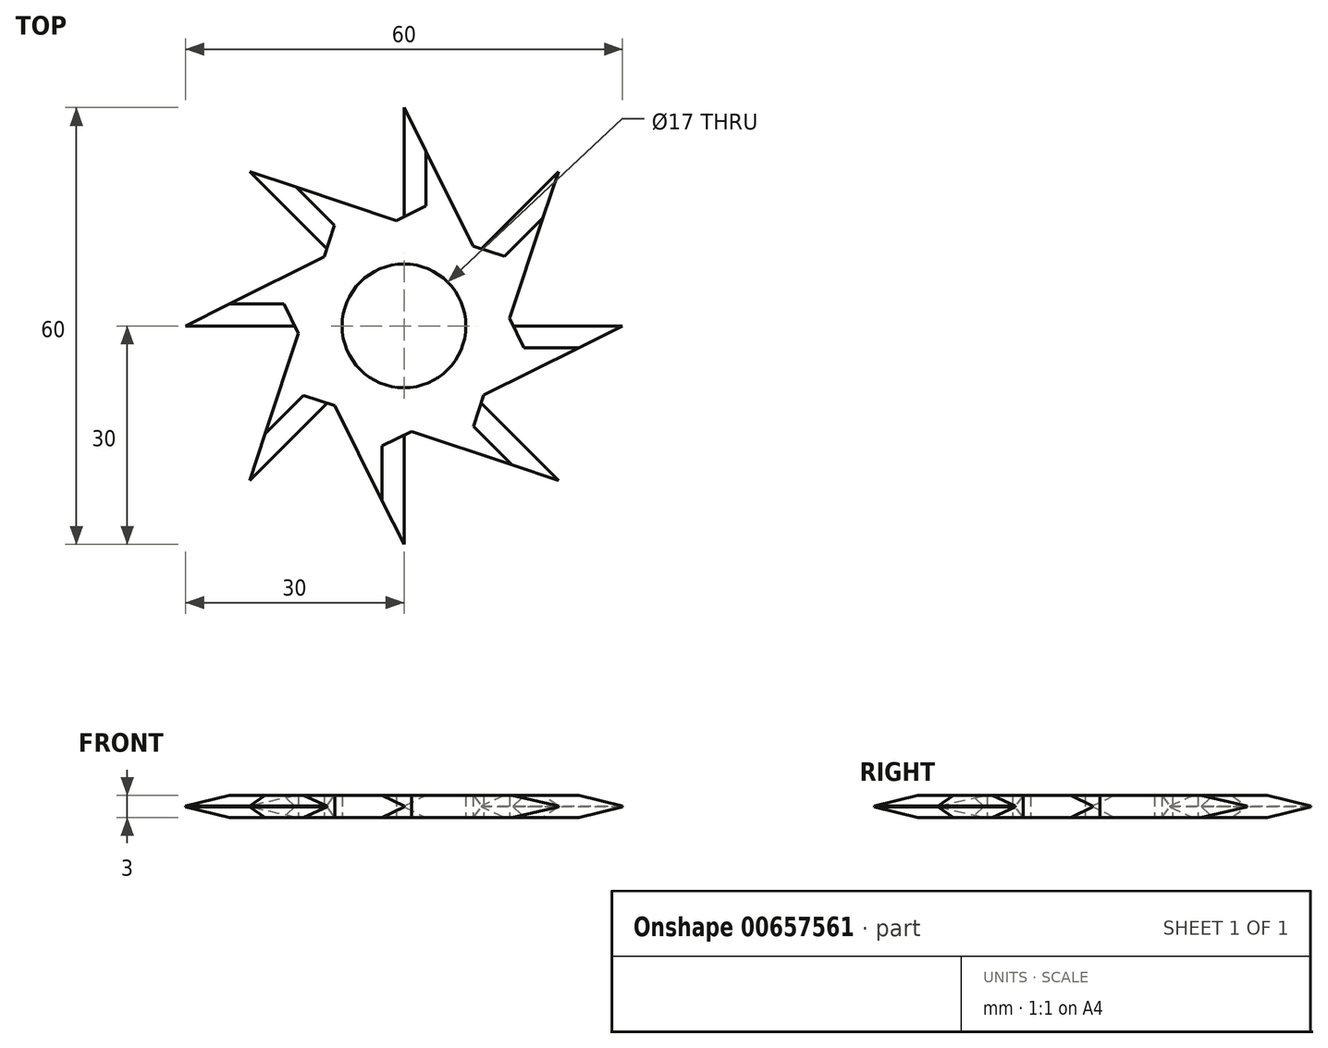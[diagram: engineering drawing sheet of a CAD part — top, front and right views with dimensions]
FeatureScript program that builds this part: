
annotation { "Feature Type Name" : "Feature", "Feature Type Description" : "" }
export const myFeature = defineFeature(function(context is Context, id is Id, definition is map)
    precondition{}
    {
        {
            var Q0;
            Q0=qCreatedBy(makeId("Top.planeOp"),FACE);
            var sketch = newSketch(context, id + "F0", { "sketchPlane" : qUnion([Q0])});
            skLineSegment(sketch, "E0", {"start": v(0, 0) * mm, "end": v(21.21, -21.21) * mm, "construction": true});
            skLineSegment(sketch, "E1", {"start": v(0, 0) * mm, "end": v(-21.21, 21.21) * mm, "construction": true});
            skLineSegment(sketch, "E2", {"start": v(0, 0) * mm, "end": v(21.21, 21.21) * mm, "construction": true});
            skLineSegment(sketch, "E3", {"start": v(21.21, 21.21) * mm, "end": v(0, 0) * mm, "construction": true});
            skLineSegment(sketch, "E4", {"start": v(0, 0) * mm, "end": v(-21.21, -21.21) * mm, "construction": true});
            skCircle(sketch, "E5", {"center": v(0, 0) * mm, "radius": 15 * mm, "construction": true});
            skCircle(sketch, "E6", {"center": v(0, 0) * mm, "radius": 30 * mm, "construction": true});
            skLineSegment(sketch, "E7", {"start": v(0, 15) * mm, "end": v(0, 30) * mm});
            skLineSegment(sketch, "E8", {"start": v(0, 30) * mm, "end": v(15, 0) * mm});
            skLineSegment(sketch, "E9", {"start": v(15, 0) * mm, "end": v(30, 0) * mm});
            skLineSegment(sketch, "E10", {"start": v(30, 0) * mm, "end": v(0, -15) * mm});
            skLineSegment(sketch, "E11", {"start": v(0, -15) * mm, "end": v(0, -30) * mm});
            skLineSegment(sketch, "E12", {"start": v(0, -30) * mm, "end": v(-15, 0) * mm});
            skLineSegment(sketch, "E13", {"start": v(-15, 0) * mm, "end": v(-30, 0) * mm});
            skLineSegment(sketch, "E14", {"start": v(-30, 0) * mm, "end": v(0, 15) * mm});
            skLineSegment(sketch, "E15", {"start": v(21.21, 21.21) * mm, "end": v(10.6, 10.6) * mm});
            skLineSegment(sketch, "E16", {"start": v(10.6, 10.6) * mm, "end": v(-21.21, 21.21) * mm});
            skLineSegment(sketch, "E17", {"start": v(-10.6, 10.6) * mm, "end": v(-21.21, 21.21) * mm});
            skLineSegment(sketch, "E18", {"start": v(-10.6, 10.6) * mm, "end": v(-21.21, -21.21) * mm});
            skLineSegment(sketch, "E19", {"start": v(-10.6, -10.6) * mm, "end": v(21.21, -21.21) * mm});
            skLineSegment(sketch, "E20", {"start": v(21.21, -21.21) * mm, "end": v(10.6, -10.6) * mm});
            skLineSegment(sketch, "E21", {"start": v(10.6, -10.6) * mm, "end": v(21.21, 21.21) * mm});
            skLineSegment(sketch, "E22", {"start": v(-21.21, -21.21) * mm, "end": v(-10.6, -10.6) * mm});
            skCircle(sketch, "E23", {"center": v(0, 0) * mm, "radius": 8.5 * mm});
            skSolve(sketch);
        }
        {
            var Q0;
            Q0=makeQuery(id+"F0.imprint","IMPRINT",FACE,{"disambiguationData":[TD([[makeQuery(id+"F0.imprint","IMPRINT",EDGE,{"derivedFrom":sQuery(id+"F0.wireOp",EDGE,"E23")}),-1.0]])]});
            var Q1;
            {var subQ5=sQuery(id+"F0.wireOp",EDGE,"E22");Q1=makeQuery(id+"F0.imprint","IMPRINT",FACE,{"disambiguationData":[TD([[makeQuery(id+"F0.imprint","IMPRINT",EDGE,{"derivedFrom":subQ5}),1.0]])]});}
            var Q2;
            {var subQ0=sQuery(id+"F0.wireOp",EDGE,"E11");Q2=makeQuery(id+"F0.imprint","IMPRINT",FACE,{"disambiguationData":[TD([[makeQuery(id+"F0.imprint","IMPRINT",EDGE,{"derivedFrom":subQ0}),-1.0]])]});}
            var Q3;
            {var subQ5=sQuery(id+"F0.wireOp",EDGE,"E20");Q3=makeQuery(id+"F0.imprint","IMPRINT",FACE,{"disambiguationData":[TD([[makeQuery(id+"F0.imprint","IMPRINT",EDGE,{"derivedFrom":subQ5}),1.0]])]});}
            var Q4;
            {var subQ0=sQuery(id+"F0.wireOp",EDGE,"E9");Q4=makeQuery(id+"F0.imprint","IMPRINT",FACE,{"disambiguationData":[TD([[makeQuery(id+"F0.imprint","IMPRINT",EDGE,{"derivedFrom":subQ0}),-1.0]])]});}
            var Q5;
            {var subQ5=sQuery(id+"F0.wireOp",EDGE,"E15");Q5=makeQuery(id+"F0.imprint","IMPRINT",FACE,{"disambiguationData":[TD([[makeQuery(id+"F0.imprint","IMPRINT",EDGE,{"derivedFrom":subQ5}),1.0]])]});}
            var Q6;
            {var subQ0=sQuery(id+"F0.wireOp",EDGE,"E7");Q6=makeQuery(id+"F0.imprint","IMPRINT",FACE,{"disambiguationData":[TD([[makeQuery(id+"F0.imprint","IMPRINT",EDGE,{"derivedFrom":subQ0}),-1.0]])]});}
            var Q7;
            {var subQ5=sQuery(id+"F0.wireOp",EDGE,"E17");Q7=makeQuery(id+"F0.imprint","IMPRINT",FACE,{"disambiguationData":[TD([[makeQuery(id+"F0.imprint","IMPRINT",EDGE,{"derivedFrom":subQ5}),-1.0]])]});}
            var Q8;
            {var subQ0=sQuery(id+"F0.wireOp",EDGE,"E13");Q8=makeQuery(id+"F0.imprint","IMPRINT",FACE,{"disambiguationData":[TD([[makeQuery(id+"F0.imprint","IMPRINT",EDGE,{"derivedFrom":subQ0}),-1.0]])]});}
            extrude(context, id + "F1", {"entities" : qUnion([Q0, Q1, Q2, Q3, Q4, Q5, Q6, Q7, Q8]), "depth" : 3 * mm, "offsetDistance" : 25 * mm});
        }
        {
            var Q0;
            Q0=makeQuery(id+"F1.opExtrude","CAP_EDGE",EDGE,{"disambiguationData":[OSD([sQuery(id+"F0.wireOp",EDGE,"E17")])],"isStart":false});
            var Q1;
            Q1=makeQuery(id+"F1.opExtrude","CAP_EDGE",EDGE,{"disambiguationData":[OSD([sQuery(id+"F0.wireOp",EDGE,"E13")])],"isStart":false});
            var Q2;
            Q2=makeQuery(id+"F1.opExtrude","CAP_EDGE",EDGE,{"disambiguationData":[OSD([sQuery(id+"F0.wireOp",EDGE,"E22")])],"isStart":false});
            var Q3;
            Q3=makeQuery(id+"F1.opExtrude","CAP_EDGE",EDGE,{"disambiguationData":[OSD([sQuery(id+"F0.wireOp",EDGE,"E11")])],"isStart":false});
            var Q4;
            Q4=makeQuery(id+"F1.opExtrude","CAP_EDGE",EDGE,{"disambiguationData":[OSD([sQuery(id+"F0.wireOp",EDGE,"E20")])],"isStart":false});
            var Q5;
            Q5=makeQuery(id+"F1.opExtrude","CAP_EDGE",EDGE,{"disambiguationData":[OSD([sQuery(id+"F0.wireOp",EDGE,"E9")])],"isStart":false});
            var Q6;
            Q6=makeQuery(id+"F1.opExtrude","CAP_EDGE",EDGE,{"disambiguationData":[OSD([sQuery(id+"F0.wireOp",EDGE,"E15")])],"isStart":false});
            var Q7;
            Q7=makeQuery(id+"F1.opExtrude","CAP_EDGE",EDGE,{"disambiguationData":[OSD([sQuery(id+"F0.wireOp",EDGE,"E7")])],"isStart":false});
            chamfer(context, id + "F2", {"entities" : qUnion([Q0, Q1, Q2, Q3, Q4, Q5, Q6, Q7]), "chamferType" : ChamferType.TWO_OFFSETS, "width1" : 1.45 * mm, "oppositeDirection" : false, "width2" : 3 * mm, "tangentPropagation" : true});
        }
        {
            var Q0;
            Q0=makeQuery(id+"F1.opExtrude","CAP_EDGE",EDGE,{"disambiguationData":[OSD([sQuery(id+"F0.wireOp",EDGE,"E11")])],"isStart":true});
            var Q1;
            Q1=makeQuery(id+"F1.opExtrude","CAP_EDGE",EDGE,{"disambiguationData":[OSD([sQuery(id+"F0.wireOp",EDGE,"E20")])],"isStart":true});
            var Q2;
            Q2=makeQuery(id+"F1.opExtrude","CAP_EDGE",EDGE,{"disambiguationData":[OSD([sQuery(id+"F0.wireOp",EDGE,"E9")])],"isStart":true});
            var Q3;
            Q3=makeQuery(id+"F1.opExtrude","CAP_EDGE",EDGE,{"disambiguationData":[OSD([sQuery(id+"F0.wireOp",EDGE,"E15")])],"isStart":true});
            var Q4;
            Q4=makeQuery(id+"F1.opExtrude","CAP_EDGE",EDGE,{"disambiguationData":[OSD([sQuery(id+"F0.wireOp",EDGE,"E7")])],"isStart":true});
            var Q5;
            Q5=makeQuery(id+"F1.opExtrude","CAP_EDGE",EDGE,{"disambiguationData":[OSD([sQuery(id+"F0.wireOp",EDGE,"E17")])],"isStart":true});
            var Q6;
            Q6=makeQuery(id+"F1.opExtrude","CAP_EDGE",EDGE,{"disambiguationData":[OSD([sQuery(id+"F0.wireOp",EDGE,"E13")])],"isStart":true});
            var Q7;
            Q7=makeQuery(id+"F1.opExtrude","CAP_EDGE",EDGE,{"disambiguationData":[OSD([sQuery(id+"F0.wireOp",EDGE,"E22")])],"isStart":true});
            chamfer(context, id + "F3", {"entities" : qUnion([Q0, Q1, Q2, Q3, Q4, Q5, Q6, Q7]), "chamferType" : ChamferType.TWO_OFFSETS, "width1" : 3 * mm, "oppositeDirection" : false, "width2" : 1.45 * mm, "tangentPropagation" : true});
        }
    });
